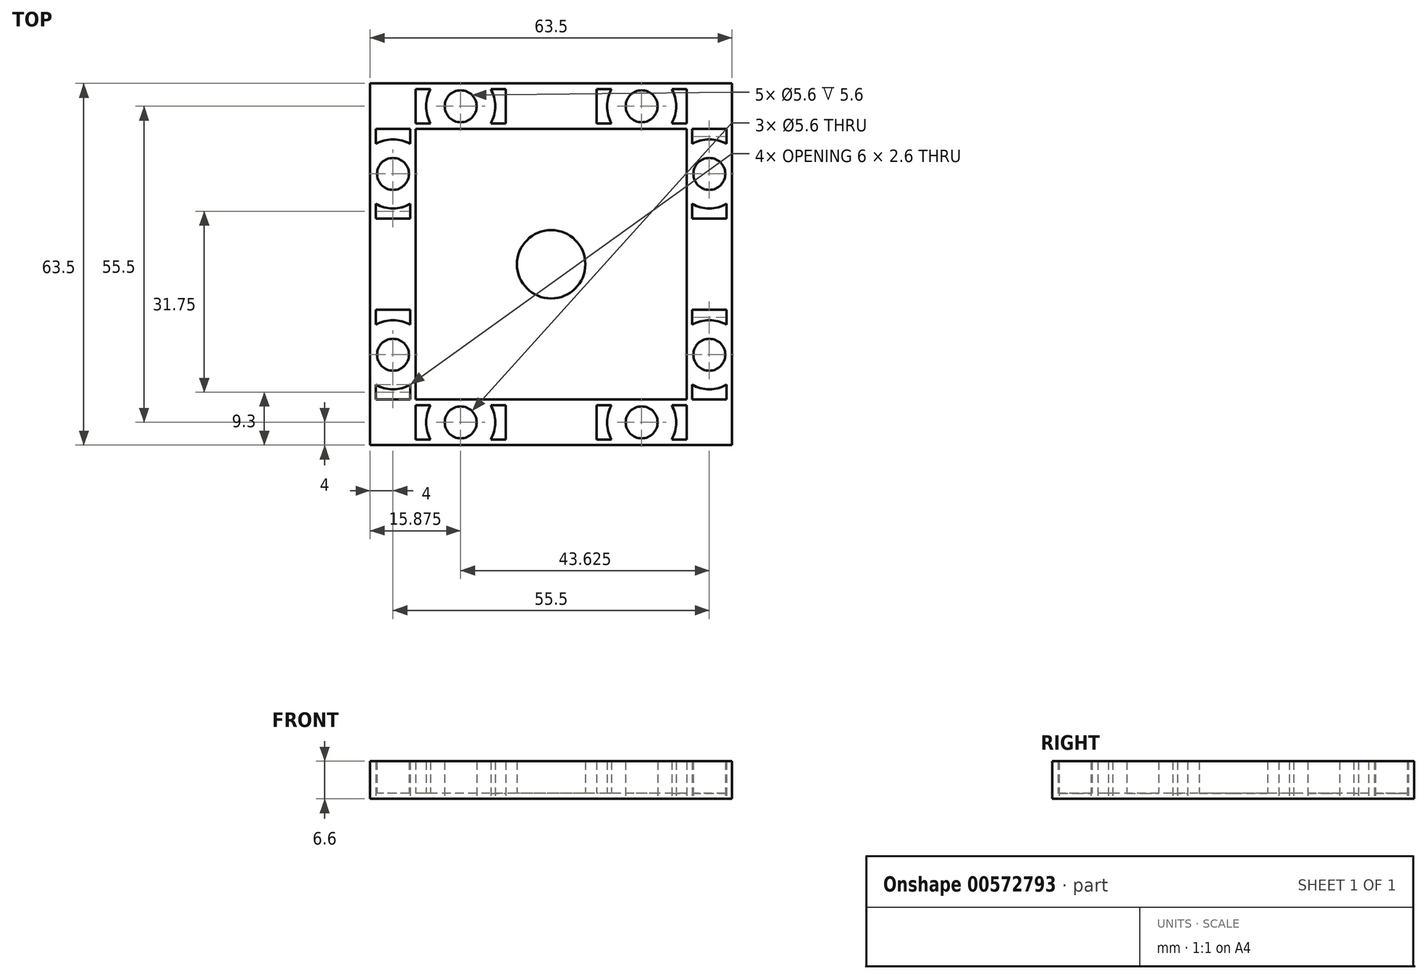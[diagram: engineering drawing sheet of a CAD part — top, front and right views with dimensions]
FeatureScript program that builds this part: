
annotation { "Feature Type Name" : "Feature", "Feature Type Description" : "" }
export const myFeature = defineFeature(function(context is Context, id is Id, definition is map)
    precondition{}
    {
        {
            var Q0;
            Q0=qCreatedBy(makeId("Top.planeOp"),FACE);
            var sketch = newSketch(context, id + "F0", { "sketchPlane" : qUnion([Q0])});
            skLineSegment(sketch, "E0.bottom", {"start": v(31.75, 31.75) * mm, "end": v(-31.75, 31.75) * mm});
            skLineSegment(sketch, "E0.top", {"start": v(31.75, -31.75) * mm, "end": v(-31.75, -31.75) * mm});
            skLineSegment(sketch, "E0.left", {"start": v(31.75, 31.75) * mm, "end": v(31.75, -31.75) * mm});
            skLineSegment(sketch, "E0.right", {"start": v(-31.75, 31.75) * mm, "end": v(-31.75, -31.75) * mm});
            skLineSegment(sketch, "E1.bottom", {"start": v(-23.75, 23.75) * mm, "end": v(23.75, 23.75) * mm});
            skLineSegment(sketch, "E1.top", {"start": v(-23.75, -23.75) * mm, "end": v(23.75, -23.75) * mm});
            skLineSegment(sketch, "E1.left", {"start": v(-23.75, 23.75) * mm, "end": v(-23.75, -23.75) * mm});
            skLineSegment(sketch, "E1.right", {"start": v(23.75, 23.75) * mm, "end": v(23.75, -23.75) * mm});
            skCircle(sketch, "E2", {"center": v(-15.87, 27.75) * mm, "radius": 2.8 * mm});
            skLineSegment(sketch, "E3", {"start": v(-15.88, 23.75) * mm, "end": v(-15.88, 31.75) * mm});
            skCircle(sketch, "E4.MirrorC", {"center": v(15.87, 27.75) * mm, "radius": 2.8 * mm});
            skLineSegment(sketch, "E5.MirrorCS", {"start": v(15.88, 23.75) * mm, "end": v(15.88, 31.75) * mm});
            skCircle(sketch, "E6.MirrorC", {"center": v(-15.87, -27.75) * mm, "radius": 2.8 * mm});
            skLineSegment(sketch, "E7.MirrorCS", {"start": v(-15.88, -23.75) * mm, "end": v(-15.88, -31.75) * mm});
            skLineSegment(sketch, "E8.MirrorCS", {"start": v(15.88, -23.75) * mm, "end": v(15.88, -31.75) * mm});
            skCircle(sketch, "E9.MirrorC", {"center": v(15.87, -27.75) * mm, "radius": 2.8 * mm});
            skLineSegment(sketch, "E10", {"start": v(-31.75, 15.88) * mm, "end": v(-23.75, 15.88) * mm});
            skCircle(sketch, "E11", {"center": v(-27.75, 15.87) * mm, "radius": 2.8 * mm});
            skCircle(sketch, "E12.MirrorC", {"center": v(27.75, 15.88) * mm, "radius": 2.8 * mm});
            skLineSegment(sketch, "E13.MirrorCS", {"start": v(31.75, 15.88) * mm, "end": v(23.75, 15.88) * mm});
            skLineSegment(sketch, "E14.MirrorCS", {"start": v(-31.75, -15.88) * mm, "end": v(-23.75, -15.88) * mm});
            skCircle(sketch, "E15.MirrorC", {"center": v(-27.75, -15.88) * mm, "radius": 2.8 * mm});
            skCircle(sketch, "E16.MirrorC", {"center": v(27.75, -15.88) * mm, "radius": 2.8 * mm});
            skLineSegment(sketch, "E17.MirrorCS", {"start": v(31.75, -15.87) * mm, "end": v(23.75, -15.87) * mm});
            skLineSegment(sketch, "E18.bottom", {"start": v(-23.75, 15.88) * mm, "end": v(-15.88, 15.88) * mm});
            skLineSegment(sketch, "E18.top", {"start": v(-23.75, 23.75) * mm, "end": v(-15.87, 23.75) * mm});
            skLineSegment(sketch, "E18.left", {"start": v(-23.75, 15.87) * mm, "end": v(-23.75, 23.75) * mm});
            skLineSegment(sketch, "E18.right", {"start": v(-15.88, 15.88) * mm, "end": v(-15.88, 23.75) * mm});
            skCircle(sketch, "E19", {"center": v(0, 0) * mm, "radius": 6 * mm});
            skLineSegment(sketch, "E20.bottom", {"start": v(-23.75, 30.75) * mm, "end": v(-21.15, 30.75) * mm});
            skLineSegment(sketch, "E20.top", {"start": v(-23.75, 24.75) * mm, "end": v(-21.15, 24.75) * mm});
            skLineSegment(sketch, "E20.left", {"start": v(-23.75, 30.75) * mm, "end": v(-23.75, 24.75) * mm});
            skArc(sketch, "E21", {"start": v(-21.15, 30.75) * mm, "mid": v(-21.94, 27.75) * mm, "end": v(-21.15, 24.75) * mm});
            skLineSegment(sketch, "E22", {"start": v(-23.75, 30.75) * mm, "end": v(-23.75, 31.75) * mm});
            skLineSegment(sketch, "E23", {"start": v(-23.75, 24.75) * mm, "end": v(-23.75, 23.75) * mm});
            skArc(sketch, "E24.MirrorCS", {"start": v(21.15, 30.75) * mm, "mid": v(21.94, 27.75) * mm, "end": v(21.15, 24.75) * mm});
            skLineSegment(sketch, "E25.MirrorCS", {"start": v(23.75, 30.75) * mm, "end": v(21.15, 30.75) * mm});
            skLineSegment(sketch, "E26.MirrorCS", {"start": v(23.75, 30.75) * mm, "end": v(23.75, 24.75) * mm});
            skLineSegment(sketch, "E27.MirrorCS", {"start": v(23.75, 24.75) * mm, "end": v(21.15, 24.75) * mm});
            skLineSegment(sketch, "E28.MirrorCS", {"start": v(23.75, -24.75) * mm, "end": v(21.15, -24.75) * mm});
            skArc(sketch, "E29.MirrorCS", {"start": v(21.15, -30.75) * mm, "mid": v(21.94, -27.75) * mm, "end": v(21.15, -24.75) * mm});
            skLineSegment(sketch, "E30.MirrorCS", {"start": v(23.75, -30.75) * mm, "end": v(23.75, -24.75) * mm});
            skLineSegment(sketch, "E31.MirrorCS", {"start": v(23.75, -30.75) * mm, "end": v(21.15, -30.75) * mm});
            skLineSegment(sketch, "E32.MirrorCS", {"start": v(-23.75, -24.75) * mm, "end": v(-21.15, -24.75) * mm});
            skLineSegment(sketch, "E33.MirrorCS", {"start": v(-23.75, -30.75) * mm, "end": v(-23.75, -24.75) * mm});
            skArc(sketch, "E34.MirrorCS", {"start": v(-21.15, -30.75) * mm, "mid": v(-21.94, -27.75) * mm, "end": v(-21.15, -24.75) * mm});
            skLineSegment(sketch, "E35.MirrorCS", {"start": v(-23.75, -30.75) * mm, "end": v(-21.15, -30.75) * mm});
            skLineSegment(sketch, "E36.bottom", {"start": v(-30.75, 23.75) * mm, "end": v(-24.75, 23.75) * mm});
            skLineSegment(sketch, "E36.left", {"start": v(-30.75, 23.75) * mm, "end": v(-30.75, 21.15) * mm});
            skLineSegment(sketch, "E36.right", {"start": v(-24.75, 23.75) * mm, "end": v(-24.75, 21.15) * mm});
            skLineSegment(sketch, "E37", {"start": v(-24.75, 23.75) * mm, "end": v(-23.75, 23.75) * mm});
            skLineSegment(sketch, "E38", {"start": v(-30.75, 23.75) * mm, "end": v(-31.75, 23.75) * mm});
            skArc(sketch, "E39", {"start": v(-24.75, 21.15) * mm, "mid": v(-27.75, 21.94) * mm, "end": v(-30.75, 21.15) * mm});
            skArc(sketch, "E40.MirrorCS", {"start": v(-24.75, -21.15) * mm, "mid": v(-27.75, -21.94) * mm, "end": v(-30.75, -21.15) * mm});
            skLineSegment(sketch, "E41.MirrorCS", {"start": v(-24.75, -23.75) * mm, "end": v(-24.75, -21.15) * mm});
            skLineSegment(sketch, "E42.MirrorCS", {"start": v(-30.75, -23.75) * mm, "end": v(-24.75, -23.75) * mm});
            skLineSegment(sketch, "E43.MirrorCS", {"start": v(-30.75, -23.75) * mm, "end": v(-30.75, -21.15) * mm});
            skArc(sketch, "E44.MirrorCS", {"start": v(24.75, 21.15) * mm, "mid": v(27.75, 21.94) * mm, "end": v(30.75, 21.15) * mm});
            skLineSegment(sketch, "E45.MirrorCS", {"start": v(30.75, 23.75) * mm, "end": v(30.75, 21.15) * mm});
            skLineSegment(sketch, "E46.MirrorCS", {"start": v(30.75, 23.75) * mm, "end": v(24.75, 23.75) * mm});
            skLineSegment(sketch, "E47.MirrorCS", {"start": v(24.75, 23.75) * mm, "end": v(24.75, 21.15) * mm});
            skArc(sketch, "E48.MirrorCS", {"start": v(24.75, -21.15) * mm, "mid": v(27.75, -21.94) * mm, "end": v(30.75, -21.15) * mm});
            skLineSegment(sketch, "E49.MirrorCS", {"start": v(30.75, -23.75) * mm, "end": v(30.75, -21.15) * mm});
            skLineSegment(sketch, "E50.MirrorCS", {"start": v(30.75, -23.75) * mm, "end": v(24.75, -23.75) * mm});
            skLineSegment(sketch, "E51.MirrorCS", {"start": v(24.75, -23.75) * mm, "end": v(24.75, -21.15) * mm});
            skArc(sketch, "E52.MirrorCS", {"start": v(-10.6, 30.75) * mm, "mid": v(-9.8, 27.75) * mm, "end": v(-10.6, 24.75) * mm});
            skLineSegment(sketch, "E53.MirrorCS", {"start": v(-8, 30.75) * mm, "end": v(-8, 24.75) * mm});
            skLineSegment(sketch, "E54.MirrorCS", {"start": v(-8, 30.75) * mm, "end": v(-10.6, 30.75) * mm});
            skLineSegment(sketch, "E55.MirrorCS", {"start": v(-8, 24.75) * mm, "end": v(-10.6, 24.75) * mm});
            skLineSegment(sketch, "E56.MirrorCS", {"start": v(8, 30.75) * mm, "end": v(10.6, 30.75) * mm});
            skArc(sketch, "E57.MirrorCS", {"start": v(10.6, 30.75) * mm, "mid": v(9.8, 27.75) * mm, "end": v(10.6, 24.75) * mm});
            skLineSegment(sketch, "E58.MirrorCS", {"start": v(8, 30.75) * mm, "end": v(8, 24.75) * mm});
            skLineSegment(sketch, "E59.MirrorCS", {"start": v(8, 24.75) * mm, "end": v(10.6, 24.75) * mm});
            skArc(sketch, "E60.MirrorCS", {"start": v(24.75, 10.6) * mm, "mid": v(27.75, 9.8) * mm, "end": v(30.75, 10.6) * mm});
            skLineSegment(sketch, "E61.MirrorCS", {"start": v(30.75, 8) * mm, "end": v(24.75, 8) * mm});
            skLineSegment(sketch, "E62.MirrorCS", {"start": v(24.75, 8) * mm, "end": v(24.75, 10.6) * mm});
            skLineSegment(sketch, "E63.MirrorCS", {"start": v(30.75, 8) * mm, "end": v(30.75, 10.6) * mm});
            skArc(sketch, "E64.MirrorCS", {"start": v(24.75, -10.6) * mm, "mid": v(27.75, -9.8) * mm, "end": v(30.75, -10.6) * mm});
            skLineSegment(sketch, "E65.MirrorCS", {"start": v(24.75, -8) * mm, "end": v(24.75, -10.6) * mm});
            skLineSegment(sketch, "E66.MirrorCS", {"start": v(30.75, -8) * mm, "end": v(24.75, -8) * mm});
            skLineSegment(sketch, "E67.MirrorCS", {"start": v(30.75, -8) * mm, "end": v(30.75, -10.6) * mm});
            skLineSegment(sketch, "E68.MirrorCS", {"start": v(8, -24.75) * mm, "end": v(10.6, -24.75) * mm});
            skArc(sketch, "E69.MirrorCS", {"start": v(10.6, -30.75) * mm, "mid": v(9.8, -27.75) * mm, "end": v(10.6, -24.75) * mm});
            skLineSegment(sketch, "E70.MirrorCS", {"start": v(8, -30.75) * mm, "end": v(8, -24.75) * mm});
            skLineSegment(sketch, "E71.MirrorCS", {"start": v(8, -30.75) * mm, "end": v(10.6, -30.75) * mm});
            skArc(sketch, "E72.MirrorCS", {"start": v(-10.6, -30.75) * mm, "mid": v(-9.8, -27.75) * mm, "end": v(-10.6, -24.75) * mm});
            skLineSegment(sketch, "E73.MirrorCS", {"start": v(-8, -24.75) * mm, "end": v(-10.6, -24.75) * mm});
            skLineSegment(sketch, "E74.MirrorCS", {"start": v(-8, -30.75) * mm, "end": v(-8, -24.75) * mm});
            skLineSegment(sketch, "E75.MirrorCS", {"start": v(-8, -30.75) * mm, "end": v(-10.6, -30.75) * mm});
            skArc(sketch, "E76.MirrorCS", {"start": v(-24.75, -10.6) * mm, "mid": v(-27.75, -9.8) * mm, "end": v(-30.75, -10.6) * mm});
            skLineSegment(sketch, "E77.MirrorCS", {"start": v(-24.75, -8) * mm, "end": v(-24.75, -10.6) * mm});
            skLineSegment(sketch, "E78.MirrorCS", {"start": v(-30.75, -8) * mm, "end": v(-24.75, -8) * mm});
            skLineSegment(sketch, "E79.MirrorCS", {"start": v(-30.75, -8) * mm, "end": v(-30.75, -10.6) * mm});
            skArc(sketch, "E80.MirrorCS", {"start": v(-24.75, 10.6) * mm, "mid": v(-27.75, 9.8) * mm, "end": v(-30.75, 10.6) * mm});
            skLineSegment(sketch, "E81.MirrorCS", {"start": v(-24.75, 8) * mm, "end": v(-24.75, 10.6) * mm});
            skLineSegment(sketch, "E82.MirrorCS", {"start": v(-30.75, 8) * mm, "end": v(-24.75, 8) * mm});
            skLineSegment(sketch, "E83.MirrorCS", {"start": v(-30.75, 8) * mm, "end": v(-30.75, 10.6) * mm});
            skLineSegment(sketch, "E84", {"start": v(0, 31.75) * mm, "end": v(0, 23.75) * mm});
            skSolve(sketch);
        }
        {
            var Q0;
            {var subQ0=sQuery(id+"F0.wireOp",EDGE,"E18.top");Q0=makeQuery(id+"F0.imprint","IMPRINT",FACE,{"disambiguationData":[TD([[makeQuery(id+"F0.imprint","IMPRINT",EDGE,{"derivedFrom":subQ0}),1.0]])]});}
            var Q1;
            {var subQ0=sQuery(id+"F0.wireOp",EDGE,"E10");var subQ5=sQuery(id+"F0.wireOp",EDGE,"E0.right");var subQ6=makeQuery(id+"F0.imprint","INTERSECT",VERTEX,{"derivedFrom":[subQ5,subQ0]});Q1=makeQuery(id+"F0.imprint","IMPRINT",FACE,{"disambiguationData":[TD([[makeQuery(id+"F0.imprint","IMPRINT",EDGE,{"disambiguationData":[TD([[subQ6,-1.0]])],"derivedFrom":subQ5}),1.0]])]});}
            var Q2;
            {var subQ7=sQuery(id+"F0.wireOp",EDGE,"E0.top");var subQ11=sQuery(id+"F0.wireOp",EDGE,"E0.right");var subQ12=makeQuery(id+"F0.imprint","INTERSECT",VERTEX,{"derivedFrom":[subQ7,subQ11]});Q2=makeQuery(id+"F0.imprint","IMPRINT",FACE,{"disambiguationData":[TD([[makeQuery(id+"F0.imprint","IMPRINT",EDGE,{"disambiguationData":[TD([[subQ12,1.0]])],"derivedFrom":subQ7}),-1.0]])]});}
            var Q3;
            {var subQ0=sQuery(id+"F0.wireOp",EDGE,"E7.MirrorCS");var subQ8=sQuery(id+"F0.wireOp",EDGE,"E0.top");var subQ9=makeQuery(id+"F0.imprint","INTERSECT",VERTEX,{"derivedFrom":[subQ8,subQ0]});Q3=makeQuery(id+"F0.imprint","IMPRINT",FACE,{"disambiguationData":[TD([[makeQuery(id+"F0.imprint","IMPRINT",EDGE,{"disambiguationData":[TD([[subQ9,1.0]])],"derivedFrom":subQ8}),-1.0]])]});}
            var Q4;
            {var subQ7=sQuery(id+"F0.wireOp",EDGE,"E0.left");var subQ8=sQuery(id+"F0.wireOp",EDGE,"E0.top");var subQ9=makeQuery(id+"F0.imprint","INTERSECT",VERTEX,{"derivedFrom":[subQ8,subQ7]});Q4=makeQuery(id+"F0.imprint","IMPRINT",FACE,{"disambiguationData":[TD([[makeQuery(id+"F0.imprint","IMPRINT",EDGE,{"disambiguationData":[TD([[subQ9,-1.0]])],"derivedFrom":subQ8}),-1.0]])]});}
            var Q5;
            {var subQ0=sQuery(id+"F0.wireOp",EDGE,"E13.MirrorCS");var subQ1=sQuery(id+"F0.wireOp",EDGE,"E0.left");var subQ2=makeQuery(id+"F0.imprint","INTERSECT",VERTEX,{"derivedFrom":[subQ1,subQ0]});Q5=makeQuery(id+"F0.imprint","IMPRINT",FACE,{"disambiguationData":[TD([[makeQuery(id+"F0.imprint","IMPRINT",EDGE,{"disambiguationData":[TD([[subQ2,-1.0]])],"derivedFrom":subQ1}),-1.0]])]});}
            var Q6;
            {var subQ7=sQuery(id+"F0.wireOp",EDGE,"E0.left");var subQ8=sQuery(id+"F0.wireOp",EDGE,"E0.bottom");var subQ9=makeQuery(id+"F0.imprint","INTERSECT",VERTEX,{"derivedFrom":[subQ8,subQ7]});Q6=makeQuery(id+"F0.imprint","IMPRINT",FACE,{"disambiguationData":[TD([[makeQuery(id+"F0.imprint","IMPRINT",EDGE,{"disambiguationData":[TD([[subQ9,-1.0]])],"derivedFrom":subQ8}),1.0]])]});}
            var Q7;
            {var subQ0=sQuery(id+"F0.wireOp",EDGE,"E3");var subQ8=sQuery(id+"F0.wireOp",EDGE,"E0.bottom");var subQ9=makeQuery(id+"F0.imprint","INTERSECT",VERTEX,{"derivedFrom":[subQ8,subQ0]});Q7=makeQuery(id+"F0.imprint","IMPRINT",FACE,{"disambiguationData":[TD([[makeQuery(id+"F0.imprint","IMPRINT",EDGE,{"disambiguationData":[TD([[subQ9,1.0]])],"derivedFrom":subQ8}),1.0]])]});}
            var Q8;
            {var subQ0=sQuery(id+"F0.wireOp",EDGE,"E3");var subQ1=sQuery(id+"F0.wireOp",EDGE,"E2");var subQ2=makeQuery(id+"F0.imprint","INTERSECT",VERTEX,{"disambiguationData":[OD(0.0)],"derivedFrom":[subQ1,subQ0]});Q8=makeQuery(id+"F0.imprint","IMPRINT",FACE,{"disambiguationData":[TD([[makeQuery(id+"F0.imprint","IMPRINT",EDGE,{"disambiguationData":[TD([[subQ2,-1.0]])],"derivedFrom":subQ1}),1.0]])]});}
            var Q9;
            {var subQ0=sQuery(id+"F0.wireOp",EDGE,"E3");var subQ1=sQuery(id+"F0.wireOp",EDGE,"E2");var subQ2=makeQuery(id+"F0.imprint","INTERSECT",VERTEX,{"disambiguationData":[OD(0.0)],"derivedFrom":[subQ1,subQ0]});Q9=makeQuery(id+"F0.imprint","IMPRINT",FACE,{"disambiguationData":[TD([[makeQuery(id+"F0.imprint","IMPRINT",EDGE,{"disambiguationData":[TD([[subQ2,1.0]])],"derivedFrom":subQ1}),1.0]])]});}
            var Q10;
            {var subQ0=sQuery(id+"F0.wireOp",EDGE,"E5.MirrorCS");var subQ1=sQuery(id+"F0.wireOp",EDGE,"E4.MirrorC");var subQ2=makeQuery(id+"F0.imprint","INTERSECT",VERTEX,{"disambiguationData":[OD(0.0)],"derivedFrom":[subQ1,subQ0]});Q10=makeQuery(id+"F0.imprint","IMPRINT",FACE,{"disambiguationData":[TD([[makeQuery(id+"F0.imprint","IMPRINT",EDGE,{"disambiguationData":[TD([[subQ2,-1.0]])],"derivedFrom":subQ1}),-1.0]])]});}
            var Q11;
            {var subQ0=sQuery(id+"F0.wireOp",EDGE,"E5.MirrorCS");var subQ1=sQuery(id+"F0.wireOp",EDGE,"E4.MirrorC");var subQ2=makeQuery(id+"F0.imprint","INTERSECT",VERTEX,{"disambiguationData":[OD(0.0)],"derivedFrom":[subQ1,subQ0]});Q11=makeQuery(id+"F0.imprint","IMPRINT",FACE,{"disambiguationData":[TD([[makeQuery(id+"F0.imprint","IMPRINT",EDGE,{"disambiguationData":[TD([[subQ2,1.0]])],"derivedFrom":subQ1}),-1.0]])]});}
            var Q12;
            {var subQ0=sQuery(id+"F0.wireOp",EDGE,"E13.MirrorCS");var subQ1=sQuery(id+"F0.wireOp",EDGE,"E12.MirrorC");var subQ2=makeQuery(id+"F0.imprint","INTERSECT",VERTEX,{"disambiguationData":[OD(0.0)],"derivedFrom":[subQ1,subQ0]});Q12=makeQuery(id+"F0.imprint","IMPRINT",FACE,{"disambiguationData":[TD([[makeQuery(id+"F0.imprint","IMPRINT",EDGE,{"disambiguationData":[TD([[subQ2,1.0]])],"derivedFrom":subQ1}),-1.0]])]});}
            var Q13;
            {var subQ0=sQuery(id+"F0.wireOp",EDGE,"E13.MirrorCS");var subQ1=sQuery(id+"F0.wireOp",EDGE,"E12.MirrorC");var subQ2=makeQuery(id+"F0.imprint","INTERSECT",VERTEX,{"disambiguationData":[OD(0.0)],"derivedFrom":[subQ1,subQ0]});Q13=makeQuery(id+"F0.imprint","IMPRINT",FACE,{"disambiguationData":[TD([[makeQuery(id+"F0.imprint","IMPRINT",EDGE,{"disambiguationData":[TD([[subQ2,-1.0]])],"derivedFrom":subQ1}),-1.0]])]});}
            var Q14;
            {var subQ0=sQuery(id+"F0.wireOp",EDGE,"E11");var subQ1=sQuery(id+"F0.wireOp",EDGE,"E10");var subQ2=makeQuery(id+"F0.imprint","INTERSECT",VERTEX,{"disambiguationData":[OD(0.0)],"derivedFrom":[subQ1,subQ0]});Q14=makeQuery(id+"F0.imprint","IMPRINT",FACE,{"disambiguationData":[TD([[makeQuery(id+"F0.imprint","IMPRINT",EDGE,{"disambiguationData":[TD([[subQ2,-1.0]])],"derivedFrom":subQ1}),1.0]])]});}
            var Q15;
            {var subQ0=sQuery(id+"F0.wireOp",EDGE,"E11");var subQ1=sQuery(id+"F0.wireOp",EDGE,"E10");var subQ2=makeQuery(id+"F0.imprint","INTERSECT",VERTEX,{"disambiguationData":[OD(0.0)],"derivedFrom":[subQ1,subQ0]});Q15=makeQuery(id+"F0.imprint","IMPRINT",FACE,{"disambiguationData":[TD([[makeQuery(id+"F0.imprint","IMPRINT",EDGE,{"disambiguationData":[TD([[subQ2,-1.0]])],"derivedFrom":subQ1}),-1.0]])]});}
            var Q16;
            {var subQ0=sQuery(id+"F0.wireOp",EDGE,"E15.MirrorC");var subQ1=sQuery(id+"F0.wireOp",EDGE,"E14.MirrorCS");var subQ2=makeQuery(id+"F0.imprint","INTERSECT",VERTEX,{"disambiguationData":[OD(0.0)],"derivedFrom":[subQ1,subQ0]});Q16=makeQuery(id+"F0.imprint","IMPRINT",FACE,{"disambiguationData":[TD([[makeQuery(id+"F0.imprint","IMPRINT",EDGE,{"disambiguationData":[TD([[subQ2,-1.0]])],"derivedFrom":subQ1}),1.0]])]});}
            var Q17;
            {var subQ0=sQuery(id+"F0.wireOp",EDGE,"E15.MirrorC");var subQ1=sQuery(id+"F0.wireOp",EDGE,"E14.MirrorCS");var subQ2=makeQuery(id+"F0.imprint","INTERSECT",VERTEX,{"disambiguationData":[OD(0.0)],"derivedFrom":[subQ1,subQ0]});Q17=makeQuery(id+"F0.imprint","IMPRINT",FACE,{"disambiguationData":[TD([[makeQuery(id+"F0.imprint","IMPRINT",EDGE,{"disambiguationData":[TD([[subQ2,-1.0]])],"derivedFrom":subQ1}),-1.0]])]});}
            var Q18;
            {var subQ0=sQuery(id+"F0.wireOp",EDGE,"E7.MirrorCS");var subQ1=sQuery(id+"F0.wireOp",EDGE,"E6.MirrorC");var subQ2=makeQuery(id+"F0.imprint","INTERSECT",VERTEX,{"disambiguationData":[OD(0.0)],"derivedFrom":[subQ1,subQ0]});Q18=makeQuery(id+"F0.imprint","IMPRINT",FACE,{"disambiguationData":[TD([[makeQuery(id+"F0.imprint","IMPRINT",EDGE,{"disambiguationData":[TD([[subQ2,-1.0]])],"derivedFrom":subQ1}),-1.0]])]});}
            var Q19;
            {var subQ0=sQuery(id+"F0.wireOp",EDGE,"E7.MirrorCS");var subQ1=sQuery(id+"F0.wireOp",EDGE,"E6.MirrorC");var subQ2=makeQuery(id+"F0.imprint","INTERSECT",VERTEX,{"disambiguationData":[OD(0.0)],"derivedFrom":[subQ1,subQ0]});Q19=makeQuery(id+"F0.imprint","IMPRINT",FACE,{"disambiguationData":[TD([[makeQuery(id+"F0.imprint","IMPRINT",EDGE,{"disambiguationData":[TD([[subQ2,1.0]])],"derivedFrom":subQ1}),-1.0]])]});}
            var Q20;
            {var subQ0=sQuery(id+"F0.wireOp",EDGE,"E9.MirrorC");var subQ1=sQuery(id+"F0.wireOp",EDGE,"E8.MirrorCS");var subQ2=makeQuery(id+"F0.imprint","INTERSECT",VERTEX,{"disambiguationData":[OD(0.0)],"derivedFrom":[subQ1,subQ0]});Q20=makeQuery(id+"F0.imprint","IMPRINT",FACE,{"disambiguationData":[TD([[makeQuery(id+"F0.imprint","IMPRINT",EDGE,{"disambiguationData":[TD([[subQ2,-1.0]])],"derivedFrom":subQ1}),1.0]])]});}
            var Q21;
            {var subQ0=sQuery(id+"F0.wireOp",EDGE,"E9.MirrorC");var subQ1=sQuery(id+"F0.wireOp",EDGE,"E8.MirrorCS");var subQ2=makeQuery(id+"F0.imprint","INTERSECT",VERTEX,{"disambiguationData":[OD(0.0)],"derivedFrom":[subQ1,subQ0]});Q21=makeQuery(id+"F0.imprint","IMPRINT",FACE,{"disambiguationData":[TD([[makeQuery(id+"F0.imprint","IMPRINT",EDGE,{"disambiguationData":[TD([[subQ2,-1.0]])],"derivedFrom":subQ1}),-1.0]])]});}
            var Q22;
            {var subQ0=sQuery(id+"F0.wireOp",EDGE,"E17.MirrorCS");var subQ1=sQuery(id+"F0.wireOp",EDGE,"E16.MirrorC");var subQ2=makeQuery(id+"F0.imprint","INTERSECT",VERTEX,{"disambiguationData":[OD(0.0)],"derivedFrom":[subQ1,subQ0]});Q22=makeQuery(id+"F0.imprint","IMPRINT",FACE,{"disambiguationData":[TD([[makeQuery(id+"F0.imprint","IMPRINT",EDGE,{"disambiguationData":[TD([[subQ2,-1.0]])],"derivedFrom":subQ1}),1.0]])]});}
            var Q23;
            {var subQ0=sQuery(id+"F0.wireOp",EDGE,"E17.MirrorCS");var subQ1=sQuery(id+"F0.wireOp",EDGE,"E16.MirrorC");var subQ2=makeQuery(id+"F0.imprint","INTERSECT",VERTEX,{"disambiguationData":[OD(0.0)],"derivedFrom":[subQ1,subQ0]});Q23=makeQuery(id+"F0.imprint","IMPRINT",FACE,{"disambiguationData":[TD([[makeQuery(id+"F0.imprint","IMPRINT",EDGE,{"disambiguationData":[TD([[subQ2,1.0]])],"derivedFrom":subQ1}),1.0]])]});}
            var Q24;
            {var subQ11=sQuery(id+"F0.wireOp",EDGE,"E18.bottom");Q24=makeQuery(id+"F0.imprint","IMPRINT",FACE,{"disambiguationData":[TD([[makeQuery(id+"F0.imprint","IMPRINT",EDGE,{"derivedFrom":subQ11}),-1.0]])]});}
            var Q25;
            Q25=makeQuery(id+"F0.imprint","IMPRINT",FACE,{"disambiguationData":[TD([[makeQuery(id+"F0.imprint","IMPRINT",EDGE,{"derivedFrom":sQuery(id+"F0.wireOp",EDGE,"E18.bottom")}),1.0]])]});
            var Q26;
            Q26=makeQuery(id+"F0.imprint","IMPRINT",FACE,{"disambiguationData":[TD([[makeQuery(id+"F0.imprint","IMPRINT",EDGE,{"derivedFrom":sQuery(id+"F0.wireOp",EDGE,"E19")}),1.0]])]});
            var Q27;
            Q27=makeQuery(id+"F0.imprint","IMPRINT",FACE,{"disambiguationData":[TD([[makeQuery(id+"F0.imprint","IMPRINT",EDGE,{"derivedFrom":sQuery(id+"F0.wireOp",EDGE,"E20.bottom")}),-1.0]])]});
            var Q28;
            Q28=makeQuery(id+"F0.imprint","IMPRINT",FACE,{"disambiguationData":[TD([[makeQuery(id+"F0.imprint","IMPRINT",EDGE,{"derivedFrom":sQuery(id+"F0.wireOp",EDGE,"E20.left")}),-1.0]])]});
            var Q29;
            {var subQ7=sQuery(id+"F0.wireOp",EDGE,"E18.left");Q29=makeQuery(id+"F0.imprint","IMPRINT",FACE,{"disambiguationData":[TD([[makeQuery(id+"F0.imprint","IMPRINT",EDGE,{"derivedFrom":subQ7}),1.0]])]});}
            var Q30;
            Q30=makeQuery(id+"F0.imprint","IMPRINT",FACE,{"disambiguationData":[TD([[makeQuery(id+"F0.imprint","IMPRINT",EDGE,{"derivedFrom":sQuery(id+"F0.wireOp",EDGE,"E36.bottom")}),-1.0]])]});
            var Q31;
            Q31=makeQuery(id+"F0.imprint","IMPRINT",FACE,{"disambiguationData":[TD([[makeQuery(id+"F0.imprint","IMPRINT",EDGE,{"derivedFrom":sQuery(id+"F0.wireOp",EDGE,"E80.MirrorCS")}),1.0]])]});
            var Q32;
            Q32=makeQuery(id+"F0.imprint","IMPRINT",FACE,{"disambiguationData":[TD([[makeQuery(id+"F0.imprint","IMPRINT",EDGE,{"derivedFrom":sQuery(id+"F0.wireOp",EDGE,"E52.MirrorCS")}),1.0]])]});
            var Q33;
            Q33=makeQuery(id+"F0.imprint","IMPRINT",FACE,{"disambiguationData":[TD([[makeQuery(id+"F0.imprint","IMPRINT",EDGE,{"derivedFrom":sQuery(id+"F0.wireOp",EDGE,"E56.MirrorCS")}),-1.0]])]});
            var Q34;
            Q34=makeQuery(id+"F0.imprint","IMPRINT",FACE,{"disambiguationData":[TD([[makeQuery(id+"F0.imprint","IMPRINT",EDGE,{"derivedFrom":sQuery(id+"F0.wireOp",EDGE,"E24.MirrorCS")}),1.0]])]});
            var Q35;
            Q35=makeQuery(id+"F0.imprint","IMPRINT",FACE,{"disambiguationData":[TD([[makeQuery(id+"F0.imprint","IMPRINT",EDGE,{"derivedFrom":sQuery(id+"F0.wireOp",EDGE,"E44.MirrorCS")}),1.0]])]});
            var Q36;
            Q36=makeQuery(id+"F0.imprint","IMPRINT",FACE,{"disambiguationData":[TD([[makeQuery(id+"F0.imprint","IMPRINT",EDGE,{"derivedFrom":sQuery(id+"F0.wireOp",EDGE,"E60.MirrorCS")}),-1.0]])]});
            var Q37;
            Q37=makeQuery(id+"F0.imprint","IMPRINT",FACE,{"disambiguationData":[TD([[makeQuery(id+"F0.imprint","IMPRINT",EDGE,{"derivedFrom":sQuery(id+"F0.wireOp",EDGE,"E28.MirrorCS")}),1.0]])]});
            var Q38;
            Q38=makeQuery(id+"F0.imprint","IMPRINT",FACE,{"disambiguationData":[TD([[makeQuery(id+"F0.imprint","IMPRINT",EDGE,{"derivedFrom":sQuery(id+"F0.wireOp",EDGE,"E68.MirrorCS")}),-1.0]])]});
            var Q39;
            Q39=makeQuery(id+"F0.imprint","IMPRINT",FACE,{"disambiguationData":[TD([[makeQuery(id+"F0.imprint","IMPRINT",EDGE,{"derivedFrom":sQuery(id+"F0.wireOp",EDGE,"E72.MirrorCS")}),-1.0]])]});
            var Q40;
            Q40=makeQuery(id+"F0.imprint","IMPRINT",FACE,{"disambiguationData":[TD([[makeQuery(id+"F0.imprint","IMPRINT",EDGE,{"derivedFrom":sQuery(id+"F0.wireOp",EDGE,"E32.MirrorCS")}),-1.0]])]});
            var Q41;
            Q41=makeQuery(id+"F0.imprint","IMPRINT",FACE,{"disambiguationData":[TD([[makeQuery(id+"F0.imprint","IMPRINT",EDGE,{"derivedFrom":sQuery(id+"F0.wireOp",EDGE,"E76.MirrorCS")}),-1.0]])]});
            var Q42;
            Q42=makeQuery(id+"F0.imprint","IMPRINT",FACE,{"disambiguationData":[TD([[makeQuery(id+"F0.imprint","IMPRINT",EDGE,{"derivedFrom":sQuery(id+"F0.wireOp",EDGE,"E40.MirrorCS")}),1.0]])]});
            var Q43;
            Q43=makeQuery(id+"F0.imprint","IMPRINT",FACE,{"disambiguationData":[TD([[makeQuery(id+"F0.imprint","IMPRINT",EDGE,{"derivedFrom":sQuery(id+"F0.wireOp",EDGE,"E48.MirrorCS")}),-1.0]])]});
            var Q44;
            Q44=makeQuery(id+"F0.imprint","IMPRINT",FACE,{"disambiguationData":[TD([[makeQuery(id+"F0.imprint","IMPRINT",EDGE,{"derivedFrom":sQuery(id+"F0.wireOp",EDGE,"E64.MirrorCS")}),1.0]])]});
            var Q45;
            Q45=makeQuery(id+"F0.imprint","IMPRINT",FACE,{"disambiguationData":[TD([[makeQuery(id+"F0.imprint","IMPRINT",EDGE,{"derivedFrom":sQuery(id+"F0.wireOp",EDGE,"E56.MirrorCS")}),1.0]])]});
            extrude(context, id + "F1", {"entities" : qUnion([Q0, Q1, Q2, Q3, Q4, Q5, Q6, Q7, Q8, Q9, Q10, Q11, Q12, Q13, Q14, Q15, Q16, Q17, Q18, Q19, Q20, Q21, Q22, Q23, Q24, Q25, Q26, Q27, Q28, Q29, Q30, Q31, Q32, Q33, Q34, Q35, Q36, Q37, Q38, Q39, Q40, Q41, Q42, Q43, Q44, Q45]), "depth" : 1 * mm, "offsetDistance" : 25 * mm});
        }
        {
            var Q0;
            Q0 = qSketchRegion(id + "F0", true);
            var Q1;
            Q1=makeQuery(id+"F0.imprint","IMPRINT",FACE,{"disambiguationData":[TD([[makeQuery(id+"F0.imprint","IMPRINT",EDGE,{"derivedFrom":sQuery(id+"F0.wireOp",EDGE,"E19")}),1.0]])]});
            var Q2;
            Q2 = qConstructionFilter(qBodyType(qCreatedBy(id + "F0" ,EDGE), BodyType.WIRE), ConstructionObject.NO);
            extrude(context, id + "F2", {"entities" : qUnion([Q0, Q1]), "operationType" : NewBodyOperationType.ADD, "surfaceEntities" : qUnion([Q2]), "depth" : 6.6 * mm, "offsetDistance" : 25 * mm});
        }
    });
